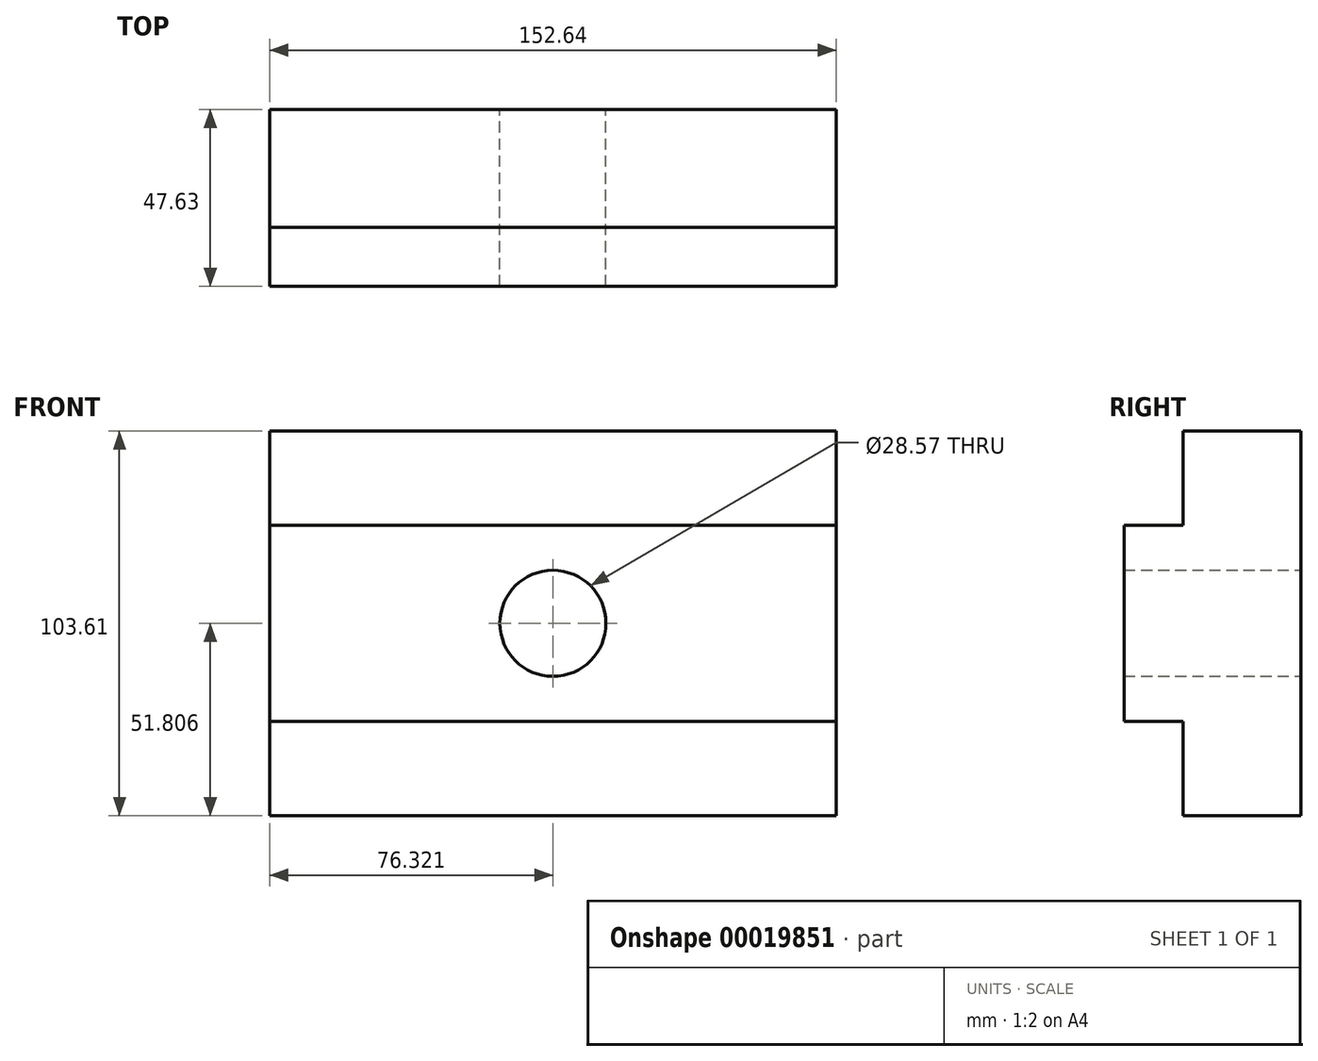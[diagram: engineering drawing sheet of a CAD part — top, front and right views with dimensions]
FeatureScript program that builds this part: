
annotation { "Feature Type Name" : "Feature", "Feature Type Description" : "" }
export const myFeature = defineFeature(function(context is Context, id is Id, definition is map)
    precondition{}
    {
        {
            var Q0;
            Q0=qCreatedBy(makeId("Front.planeOp"),FACE);
            var sketch = newSketch(context, id + "F0", { "sketchPlane" : qUnion([Q0])});
            skLineSegment(sketch, "E0.bottom", {"start": v(-70.59, 100.41) * mm, "end": v(81.81, 100.41) * mm});
            skLineSegment(sketch, "E0.top", {"start": v(-70.59, 49.61) * mm, "end": v(81.81, 49.61) * mm});
            skLineSegment(sketch, "E0.left", {"start": v(-70.59, 100.41) * mm, "end": v(-70.59, 49.61) * mm});
            skLineSegment(sketch, "E0.right", {"start": v(81.81, 100.41) * mm, "end": v(81.81, 49.61) * mm});
            skLineSegment(sketch, "E1", {"start": v(-70.59, 100.41) * mm, "end": v(-70.59, 125.81) * mm});
            skLineSegment(sketch, "E2", {"start": v(-70.59, 49.61) * mm, "end": v(-70.59, 24.21) * mm});
            skLineSegment(sketch, "E3.bottom", {"start": v(-70.59, 125.81) * mm, "end": v(82.05, 125.81) * mm});
            skLineSegment(sketch, "E3.top", {"start": v(-70.59, 22.2) * mm, "end": v(82.05, 22.2) * mm});
            skLineSegment(sketch, "E3.left", {"start": v(-70.59, 125.81) * mm, "end": v(-70.59, 22.2) * mm});
            skLineSegment(sketch, "E3.right", {"start": v(82.05, 125.81) * mm, "end": v(82.05, 22.2) * mm});
            skCircle(sketch, "E4", {"center": v(5.73, 74) * mm, "radius": 14.29 * mm});
            skSolve(sketch);
        }
        {
            var Q0;
            Q0 = qSketchRegion(id + "F0", true);
            extrude(context, id + "F1", {"entities" : qUnion([Q0]), "depth" : 31.75 * mm});
        }
        {
            var Q0;
            Q0=makeQuery(id+"F1.opExtrude","CAP_FACE",FACE,{"disambiguationData":[OSD([sQuery(id+"F0.wireOp",EDGE,"E3.bottom"),sQuery(id+"F0.wireOp",EDGE,"E3.top"),sQuery(id+"F0.wireOp",EDGE,"E3.left"),sQuery(id+"F0.wireOp",EDGE,"E3.right"),sQuery(id+"F0.wireOp",EDGE,"E4")])],"isStart":false});
            var sketch = newSketch(context, id + "F2", { "sketchPlane" : qUnion([Q0])});
            skLineSegment(sketch, "E5", {"start": v(-70.59, 125.81) * mm, "end": v(-70.59, 100.41) * mm});
            skLineSegment(sketch, "E6", {"start": v(-70.59, 22.2) * mm, "end": v(-70.59, 47.6) * mm});
            skLineSegment(sketch, "E7", {"start": v(-70.59, 47.6) * mm, "end": v(82.05, 47.6) * mm});
            skLineSegment(sketch, "E8", {"start": v(82.05, 47.6) * mm, "end": v(82.05, 100.41) * mm});
            skLineSegment(sketch, "E9", {"start": v(-70.59, 100.41) * mm, "end": v(82.05, 100.41) * mm});
            skLineSegment(sketch, "E10", {"start": v(-70.59, 100.41) * mm, "end": v(-70.59, 47.6) * mm});
            skSolve(sketch);
        }
        {
            var Q0;
            Q0=makeQuery(id+"F2.imprint","IMPRINT",FACE,{"disambiguationData":[TD([[makeQuery(id+"F2.imprint","IMPRINT",EDGE,{"derivedFrom":sQuery(id+"F2.wireOp",EDGE,"E7")}),1.0]])]});
            extrude(context, id + "F3", {"entities" : qUnion([Q0]), "operationType" : NewBodyOperationType.ADD, "depth" : 15.88 * mm});
        }
    });
